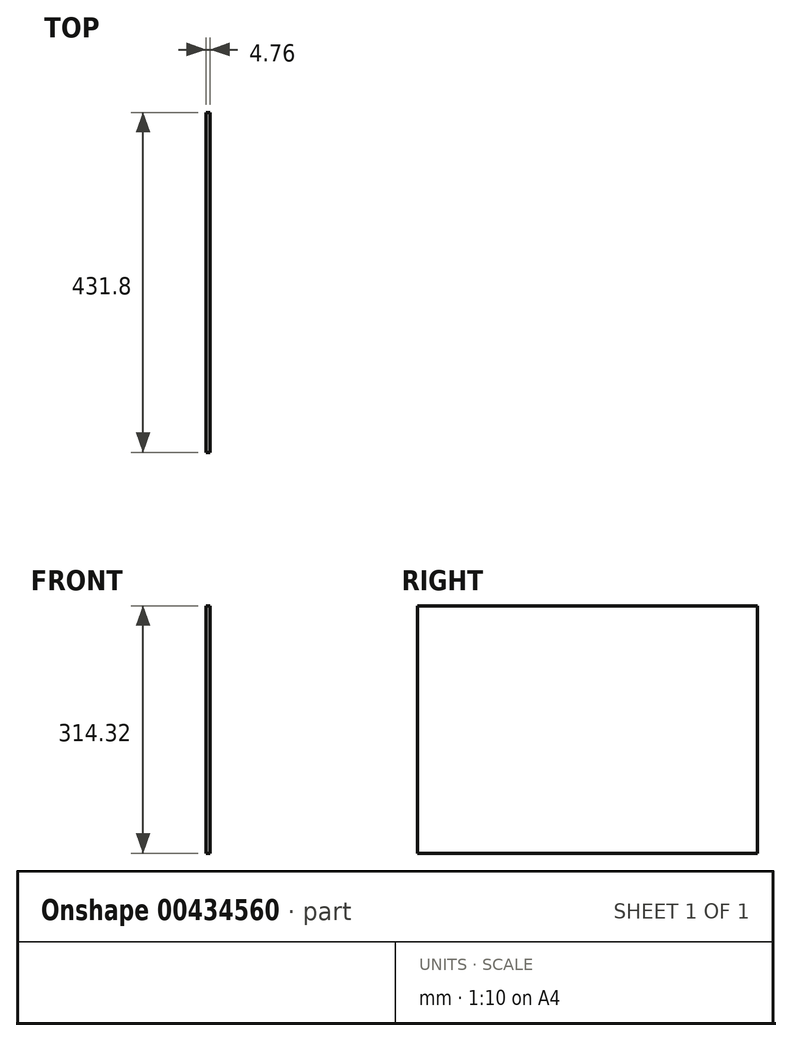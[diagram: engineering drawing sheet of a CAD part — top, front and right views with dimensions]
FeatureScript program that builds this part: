
annotation { "Feature Type Name" : "Feature", "Feature Type Description" : "" }
export const myFeature = defineFeature(function(context is Context, id is Id, definition is map)
    precondition{}
    {
        {
            var Q0;
            Q0=qCreatedBy(makeId("Right.planeOp"),FACE);
            var sketch = newSketch(context, id + "F0", { "sketchPlane" : qUnion([Q0])});
            skLineSegment(sketch, "E0.bottom", {"start": v(-342.36, 100.36) * mm, "end": v(89.44, 100.36) * mm});
            skLineSegment(sketch, "E0.top", {"start": v(-342.36, -213.96) * mm, "end": v(89.44, -213.96) * mm});
            skLineSegment(sketch, "E0.left", {"start": v(-342.36, 100.36) * mm, "end": v(-342.36, -213.96) * mm});
            skLineSegment(sketch, "E0.right", {"start": v(89.44, 100.36) * mm, "end": v(89.44, -213.96) * mm});
            skSolve(sketch);
        }
        {
            var Q0;
            Q0=makeQuery(id+"F0.imprint","IMPRINT",FACE,{"disambiguationData":[TD([[makeQuery(id+"F0.imprint","IMPRINT",EDGE,{"derivedFrom":sQuery(id+"F0.wireOp",EDGE,"E0.bottom")}),-1.0]])]});
            extrude(context, id + "F1", {"entities" : qUnion([Q0]), "depth" : 4.76 * mm});
        }
    });
